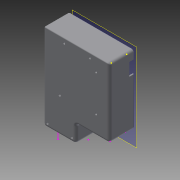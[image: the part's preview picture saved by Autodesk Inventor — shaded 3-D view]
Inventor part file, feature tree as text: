
AUTODESK INVENTOR PART (.ipt)
format: ipt  version: 2014 (Build 180170000, 170)  size: 422,912 bytes
history: native  units: mm
features: extrude x10, sketch x10, other x4, fillet x4, projected_geometry x3
ambient origin geometry x8: Origin, YZ Plane, XZ Plane, XY Plane, X Axis, Y Axis, Z Axis, Center Point
bodies: Body1 (feature_tree)
feature tree (31):
  other  "ソリッド1"
  extrude  "押し出し1"  TaperAngle=0.0deg  [1 undecoded]
  extrude  "押し出し2"  Depth=28.2mm
  extrude  "押し出し3"  Depth=5.0mm
  sketch  "スケッチ4"
  extrude  "押し出し4"  Depth=2.6mm
  extrude  "押し出し6"  Depth=2.6mm
  extrude  "押し出し7"  Depth=2.6mm
  fillet  "フィレット1"  Radius=2.0mm
  other  "作業平面1"
  extrude  "押し出し8"  Depth=1.4mm
  sketch  "スケッチ11"
  fillet  "フィレット4"  Radius=1.4mm
  fillet  "フィレット5"  Radius=1.4mm
  extrude  "押し出し12"  Depth=7.0mm TaperAngle=0.0deg
  fillet  "フィレット8"  Radius=52.0mm
  extrude  "押し出し13"  TaperAngle=0.0deg  [1 undecoded]
  extrude  "押し出し14"  Depth=40.0mm
  other  "面の勾配5"
  other  "面の勾配6"
  sketch  "スケッチ1"
  sketch  "スケッチ2"
  sketch  "スケッチ5"
  sketch  "スケッチ7"
  sketch  "スケッチ8"
  sketch  "スケッチ15"
  projected_geometry  "投影ループ5"
  projected_geometry  "投影ループ6"
  sketch  "スケッチ16"
  sketch  "スケッチ18"
  projected_geometry  "投影ループ7"
note: 2 required parameter values undecoded (feature->parameter linkage not recoverable at this tier; creation-order binding heuristic only, values carry confidence <= 0.55)
